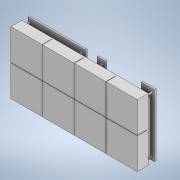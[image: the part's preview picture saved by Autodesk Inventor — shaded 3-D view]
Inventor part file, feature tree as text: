
AUTODESK INVENTOR PART (.ipt)
format: ipt  version: 2021 (Build 250183000, 183)  size: 395,264 bytes
history: native  units: mm
features: sketch x17, extrude x15, hole x1, fillet x1, chamfer x1
ambient origin geometry x8: Origin, YZ Plane, XZ Plane, XY Plane, X Axis, Y Axis, Z Axis, Center Point
bodies: Solid1 (feature_tree)
feature tree (35):
  extrude  "Extrusion1"  Depth=40.0mm
  extrude  "Extrusion2"  Depth=20.0mm
  extrude  "Extrusion3"  Depth=19.9mm
  extrude  "Extrusion4"  Depth=6.0mm TaperAngle=0.0deg
  extrude  "Extrusion5"  Depth=0.2mm
  extrude  "Extrusion6"  Depth=19.9mm
  hole  "Hole1"  [1 undecoded]
  extrude  "Extrusion8"  Depth=6.0mm TaperAngle=0.0deg
  sketch  "Sketch10"  dims[d19=0.5mm d20=2.0mm]
  extrude  "Extrusion9"  Depth=2.0mm
  extrude  "Extrusion10"  Depth=0.5mm
  extrude  "Extrusion11"  Depth=1.0mm
  extrude  "Extrusion12"  Depth=1.0mm TaperAngle=0.0deg
  extrude  "Extrusion13"  Depth=7.5mm
  extrude  "Extrusion14"  Depth=1.0mm TaperAngle=0.0deg
  fillet  "Fillet1"  Radius=5.0mm
  extrude  "Extrusion15"  Depth=5.0mm
  chamfer  "Chamfer1"  Distance=5.0mm
  extrude  "Extrusion16"  Depth=5.0mm
  sketch  "Sketch1"  dims[d0=81.0mm d1=40.0mm]
  sketch  "Sketch2"  dims[d2=20.0mm d3=40.5mm]
  sketch  "Sketch3"  dims[d4=7.0mm d5=0.0mm d6=19.9mm]
  sketch  "Sketch4"  dims[d7=19.9mm d8=6.0mm d9=0.0mm]
  sketch  "Sketch5"  dims[d10=0.2mm d11=0.2mm]
  sketch  "Sketch6"  dims[d12=0.2mm d13=19.9mm]
  sketch  "Sketch8"  dims[d14=19.9mm d15=40.4mm]
  sketch  "Sketch9"  dims[d16=40.4mm d17=6.0mm d18=0.0mm]
  sketch  "Sketch11"  dims[d21=2.0mm d22=0.5mm]
  sketch  "Sketch12"  dims[d23=1.0mm d24=1.0mm]
  sketch  "Sketch13"  dims[d25=5.0mm d26=0.0mm d27=1.0mm d28=0.0mm]
  sketch  "Sketch14"  dims[d29=7.5mm d30=3.75mm]
  sketch  "Sketch15"  dims[d31=18.0mm d32=1.0mm d33=0.0mm d39=5.0mm]
  sketch  "Sketch16"  dims[d40=35.0mm d41=5.0mm]
  sketch  "Sketch17"  dims[d42=5.0mm]
  sketch  "Sketch18"  dims[d43=40.5mm d44=5.0mm d45=5.0mm d46=76.03mm d47=76.03mm d48=35.0mm d49=23.0mm d50=23.0mm d51=37.0mm d52=37.0mm d53=34.0mm d54=34.0mm d55=47.0mm d56=47.0mm d57=2.0mm d58=6.0mm d59=4.0mm d60=2.0mm d61=90.0deg d62=1.0mm d63=20.594885mm d64=0.5mm d65=5.0mm d66=0.0mm d67=4.2mm d68=13.0mm d69=3.0mm d70=4.2mm d71=13.0mm d72=3.0mm d73=1.0mm d74=0.0mm d75=5.2mm d76=12.44mm d77=23.1mm d78=4.5mm d79=0.0mm d80=1.0mm d81=1.0mm d82=1.0mm d83=3.0mm d84=2.0mm d85=0.0mm d86=22.4mm d87=37.6mm d88=43.0mm d89=58.3mm d90=2.7mm d91=6.2mm d92=0.3mm d93=0.3mm d94=0.3mm d95=0.3mm d96=0.3mm d97=0.3mm d98=6.0mm d99=0.0mm d100=1.0mm d101=1.0mm d102=1.0mm d103=1.0mm d104=1.0mm d105=1.0mm d106=1.0mm d107=1.0mm d108=5.0mm d109=3.0mm d110=0.0mm d111=40.5mm d112=15.0mm d113=6.0mm d114=8.3mm d115=0.0mm d116=0.5mm d117=3.2mm d118=3.2mm d119=3.2mm d120=3.2mm d121=1.0mm d122=0.0mm d123=1.0mm d124=2.0mm d125=45.0deg d126=1.0mm d127=1.0mm d128=1.0mm d129=0.0mm]
note: 1 required parameter value undecoded (feature->parameter linkage not recoverable at this tier; creation-order binding heuristic only, values carry confidence <= 0.55)
